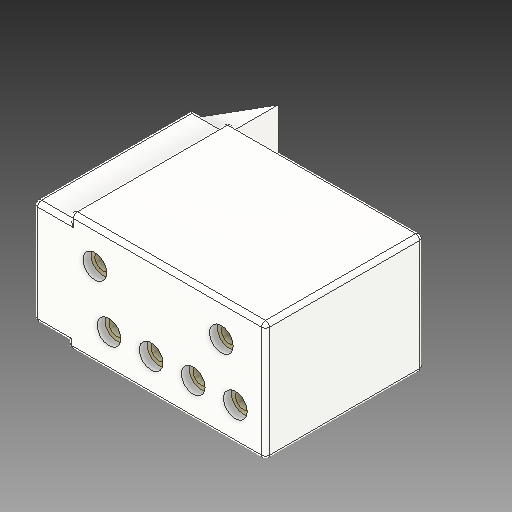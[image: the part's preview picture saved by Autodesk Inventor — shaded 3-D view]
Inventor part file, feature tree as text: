
AUTODESK INVENTOR PART (.ipt)
format: ipt  version: 2019 (Build 230136000, 136)  size: 414,208 bytes
history: native  units: in
note: dims shown in document units (in); Inventor stores cm internally (conversion verified against a paired STEP export)
features: sketch x12, extrude x6, projected_geometry x3, chamfer x1, fillet x1
ambient origin geometry x8: Origin, YZ Plane, XZ Plane, XY Plane, X Axis, Y Axis, Z Axis, Center Point
bodies: Solid1 (feature_tree), Solid2 (feature_tree)
feature tree (23):
  extrude  "Extrusion1"  Depth=0.4724in TaperAngle=0.0deg
  extrude  "Extrusion2"  Depth=0.0787in
  extrude  "Extrusion3"  Depth=0.0787in
  extrude  "Extrusion4"  Depth=0.2756in
  chamfer  "Chamfer1"  Distance=0.2756in
  extrude  "Extrusion5"  Depth=0.0591in
  extrude  "Extrusion6"  Depth=0.0591in
  fillet  "Fillet1"  Radius=0.0591in
  sketch  "Sketch7"  dims[d15=0.1181in]
  sketch  "Sketch8"  dims[d16=0.1181in]
  sketch  "Sketch9"  dims[d17=0.1181in d18=0.2756in d19=0.0in]
  sketch  "Sketch10"  dims[d20=0.0197in d21=0.0787in d22=45.0deg d23=0.0591in]
  sketch  "Sketch11"  dims[d24=0.0591in d25=0.0591in d26=0.0591in]
  sketch  "Sketch12"  dims[d27=0.0591in d28=0.0591in d29=0.0098in d30=0.0098in d31=0.0098in d32=0.0098in d33=0.0098in d34=0.0098in d35=0.4528in d36=0.0in d37=0.0787in d38=0.0787in d39=0.0787in d40=0.0787in d41=0.0787in d42=0.0787in d43=0.2756in d44=0.0in d45=0.0197in]
  sketch  "Sketch1"  dims[d2=0.7874in d3=0.0in d4=0.4724in d5=0.0in]
  sketch  "Sketch2"  dims[d6=0.0787in d7=0.0787in]
  sketch  "Sketch3"  dims[d8=120.0deg d9=0.0787in]
  projected_geometry  "Projected Loop1"
  sketch  "Sketch4"  dims[d10=0.2756in d11=0.0in d12=0.1181in]
  projected_geometry  "Projected Loop2"
  sketch  "Sketch5"  dims[d13=0.1181in]
  sketch  "Sketch6"  dims[d14=0.1181in]
  projected_geometry  "Projected Loop3"
